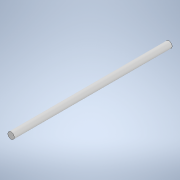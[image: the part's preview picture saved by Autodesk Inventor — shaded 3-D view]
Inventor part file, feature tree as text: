
AUTODESK INVENTOR PART (.ipt)
format: ipt  version: 2021 (Build 250183000, 183)  size: 92,160 bytes
history: native  units: mm
features: extrude x1, sketch x1
ambient origin geometry x8: Origin, YZ Plane, XZ Plane, XY Plane, X Axis, Y Axis, Z Axis, Center Point
bodies: Solid1 (feature_tree)
feature tree (2):
  extrude  "Extrusion1"  Depth=74.5mm TaperAngle=0.0deg
  sketch  "Sketch1"  dims[d0=3.0mm d1=74.5mm d2=0.0mm]
